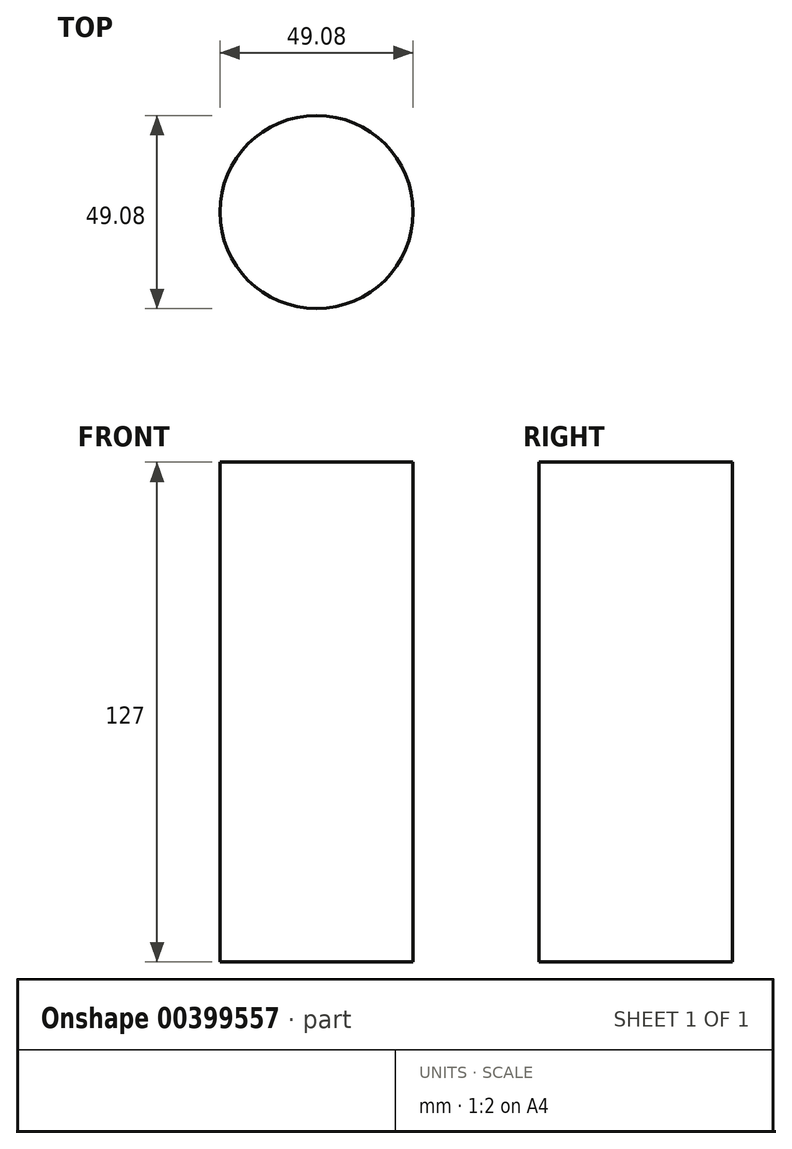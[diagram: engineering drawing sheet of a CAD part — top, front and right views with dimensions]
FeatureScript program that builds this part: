
annotation { "Feature Type Name" : "Feature", "Feature Type Description" : "" }
export const myFeature = defineFeature(function(context is Context, id is Id, definition is map)
    precondition{}
    {
        {
            var Q0;
            Q0=qCreatedBy(makeId("Top.planeOp"),FACE);
            var sketch = newSketch(context, id + "F0", { "sketchPlane" : qUnion([Q0])});
            skCircle(sketch, "E0", {"center": v(0, 0) * mm, "radius": 24.54 * mm});
            skSolve(sketch);
        }
        {
            var Q0;
            Q0=makeQuery(id+"F0.imprint","IMPRINT",FACE,{"disambiguationData":[TD([[makeQuery(id+"F0.imprint","IMPRINT",EDGE,{"derivedFrom":sQuery(id+"F0.wireOp",EDGE,"E0")}),1.0]])]});
            extrude(context, id + "F1", {"entities" : qUnion([Q0]), "depth" : 127 * mm});
        }
    });
